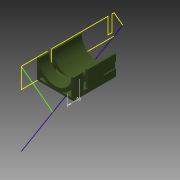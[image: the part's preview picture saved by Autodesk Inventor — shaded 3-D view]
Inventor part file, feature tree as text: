
AUTODESK INVENTOR PART (.ipt)
format: ipt  version: 2013 (Build 170138000, 138)  size: 276,480 bytes
history: native  units: mm
features: sketch x14, extrude x12, other x1, hole x1
ambient origin geometry x8: Origin, YZ Plane, XZ Plane, XY Plane, X Axis, Y Axis, Z Axis, Center Point
feature tree (28):
  other  "ソリッド1"
  extrude  "押し出し1"  Depth=90.0mm
  extrude  "押し出し2"  Depth=50.0mm
  extrude  "押し出し3"  Depth=5.0mm
  extrude  "押し出し4"  Depth=85.0mm
  extrude  "押し出し6"  Depth=5.0mm
  sketch  "スケッチ9"
  hole  "穴1"  [1 undecoded]
  extrude  "押し出し8"  Depth=10.0mm
  extrude  "押し出し9"  Depth=90.0mm
  extrude  "押し出し10"  Depth=230.0mm TaperAngle=0.0deg
  extrude  "押し出し11"  Depth=225.0mm TaperAngle=0.0deg
  extrude  "押し出し12"  Depth=5.0mm TaperAngle=0.0deg
  extrude  "押し出し13"  Depth=65.0mm
  extrude  "押し出し14"  Depth=10.0mm
  sketch  "スケッチ1"
  sketch  "スケッチ2"
  sketch  "スケッチ3"
  sketch  "スケッチ4"
  sketch  "スケッチ6"
  sketch  "スケッチ11"
  sketch  "スケッチ12"
  sketch  "スケッチ13"
  sketch  "スケッチ14"
  sketch  "スケッチ16"
  sketch  "スケッチ17"
  sketch  "スケッチ18"
  sketch  "スケッチ19"
note: 1 required parameter value undecoded (feature->parameter linkage not recoverable at this tier; creation-order binding heuristic only, values carry confidence <= 0.55)
